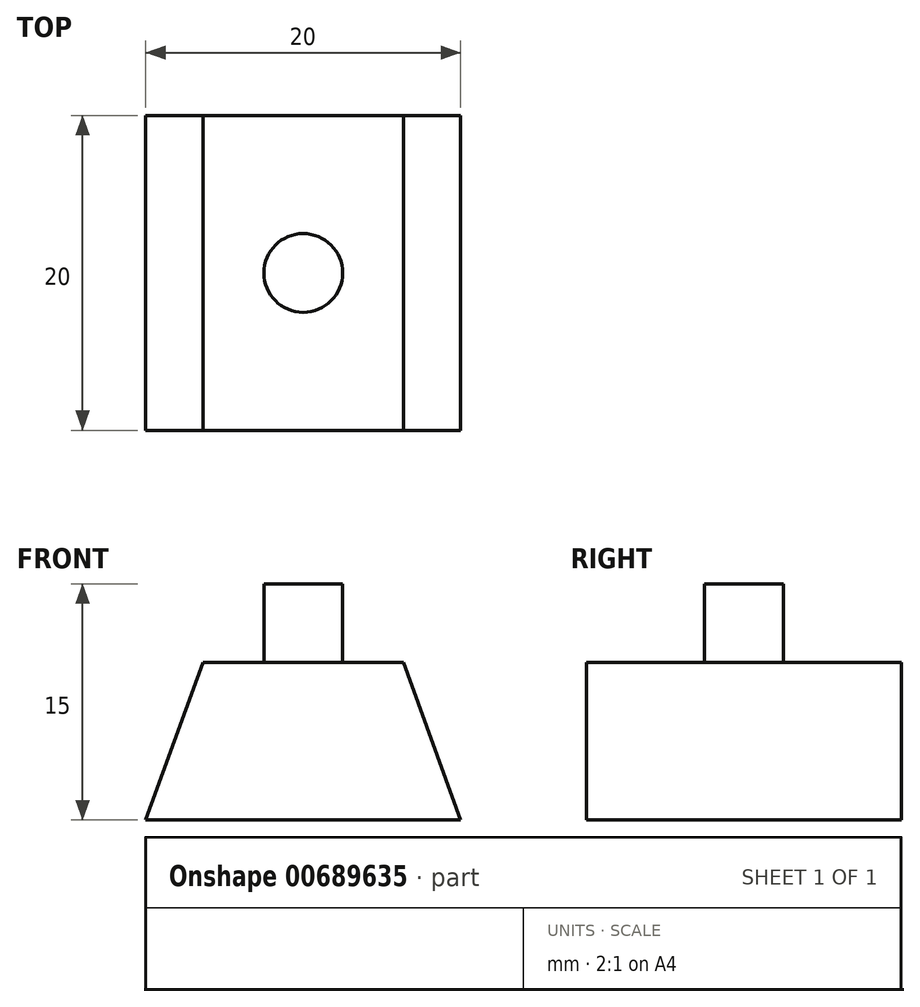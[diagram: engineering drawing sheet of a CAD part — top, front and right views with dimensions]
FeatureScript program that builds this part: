
annotation { "Feature Type Name" : "Feature", "Feature Type Description" : "" }
export const myFeature = defineFeature(function(context is Context, id is Id, definition is map)
    precondition{}
    {
        {
            var Q0;
            Q0=qCreatedBy(makeId("Front.planeOp"),FACE);
            var sketch = newSketch(context, id + "F0", { "sketchPlane" : qUnion([Q0])});
            skLineSegment(sketch, "E0", {"start": v(-13.68, -0.7) * mm, "end": v(6.32, -0.7) * mm});
            skLineSegment(sketch, "E1", {"start": v(6.32, -0.7) * mm, "end": v(2.68, 9.3) * mm});
            skLineSegment(sketch, "E2", {"start": v(2.68, 9.3) * mm, "end": v(-10.04, 9.3) * mm});
            skLineSegment(sketch, "E3", {"start": v(-10.04, 9.3) * mm, "end": v(-13.68, -0.7) * mm});
            skSolve(sketch);
        }
        {
            var Q0;
            Q0=makeQuery(id+"F0.imprint","IMPRINT",FACE,{"disambiguationData":[TD([[makeQuery(id+"F0.imprint","IMPRINT",EDGE,{"derivedFrom":sQuery(id+"F0.wireOp",EDGE,"E0")}),1.0]])]});
            extrude(context, id + "F1", {"entities" : qUnion([Q0]), "oppositeDirection" : true, "depth" : 20 * mm, "offsetDistance" : 25 * mm});
        }
        {
            var Q0;
            Q0=makeQuery(id+"F1.opExtrude","SWEPT_FACE",FACE,{"disambiguationData":[OSD([sQuery(id+"F0.wireOp",EDGE,"E2")])]});
            var sketch = newSketch(context, id + "F2", { "sketchPlane" : qUnion([Q0])});
            skCircle(sketch, "E4", {"center": v(-3.68, 10) * mm, "radius": 2.5 * mm});
            skSolve(sketch);
        }
        {
            var Q0;
            Q0=makeQuery(id+"F2.imprint","IMPRINT",FACE,{"disambiguationData":[TD([[makeQuery(id+"F2.imprint","IMPRINT",EDGE,{"derivedFrom":sQuery(id+"F2.wireOp",EDGE,"E4")}),1.0]])]});
            extrude(context, id + "F3", {"entities" : qUnion([Q0]), "operationType" : NewBodyOperationType.ADD, "depth" : 5 * mm, "offsetDistance" : 25 * mm});
        }
    });
